# Revit family: Public Health - Drainage - Straight (Circle)
name_source: partatom
category: Generic Models
revit_build: Autodesk Revit 2018 (Build: 20190510_1515(x64)
units: mm (PartAtom-declared; Revit-internal decimal feet)

## family parameters
Always vertical = Yes
Can host rebar = No
Cut with Voids When Loaded = Yes
Part Type = Normal
Room Calculation Point = No
Round Connector Dimension = Use Diameter
Shared = Yes

## types (8) — shared parameters
Opening in Slab = 215 mm
Pipe Diameter = 100 mm  [stored 0.328084 ft]

## per-type parameters (varying)
| type | Model | Pipe Type |
| 100 Diameter - 215 Opening - SVP | SVP | Pipe - SVP |
| 100 Diameter - 215 Opening - AAV | AAV | Pipe - AAV |
| 100 Diameter - 215 Opening - Gully | GUL | Pipe - Gully |
| 100 Diameter - 215 Opening - Future Gully | FGC | Pipe - Future Gully |
| 100 Diameter - 215 Opening - SS | SS | Pipe - SS |
| 100 Diameter - 215 Opening - Dry Riser | Riser | Pipe - Dry Riser |
| 100 Diameter - 215 Opening - FDP | FDP | Pipe - DP |
| 100 Diameter - 215 Opening - DP | DP | Pipe - DP |

note: [stored X ft] marks values corroborated as IEEE doubles in the binary element streams (Revit-internal decimal feet)

## geometry (parser evidence)
native form markers: Sweep x5
no freeform markers — native parametric forms only
